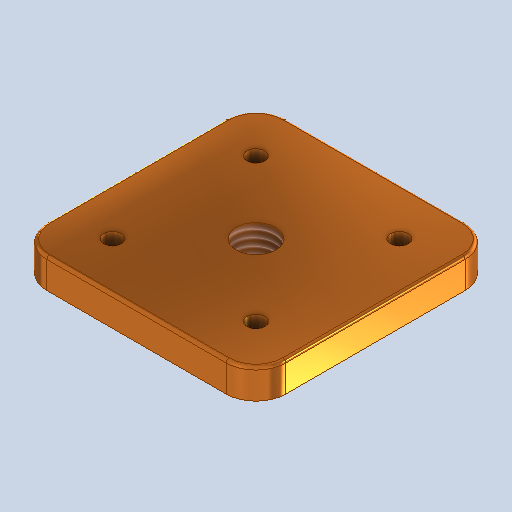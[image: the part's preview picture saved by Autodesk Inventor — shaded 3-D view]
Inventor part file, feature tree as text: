
AUTODESK INVENTOR PART (.ipt)
format: ipt  version: 2025.1 (Build 291241000, 241)  size: 265,728 bytes
history: native  units: mm
features: sketch x2, hole x2, fillet x2, extrude x1
ambient origin geometry x8: Origin, YZ Plane, XZ Plane, XY Plane, X Axis, Y Axis, Z Axis, Center Point
bodies: Solid1 (feature_tree)
feature tree (7):
  extrude  "Extrusion1"  Depth=40.0mm
  sketch  "Sketch2"  dims[d2=5.0mm d3=0.0mm d4=24.0mm d5=12.0mm d6=24.0mm d7=12.0mm d8=3.0mm d9=6.0mm d10=4.0mm d11=2.0mm d12=90.0deg d13=8.0mm d14=0.0mm d15=6.647mm d16=16.0mm d17=4.0mm d18=2.0mm d19=90.0deg d20=8.0mm d21=0.0mm d22=5.0mm d23=0.5mm]
  hole  "Hole1"  [1 undecoded]
  hole  "Hole2"  [1 undecoded]
  fillet  "Fillet1"  Radius=24.0mm
  fillet  "Fillet2"  Radius=12.0mm
  sketch  "Sketch1"  dims[d0=40.0mm d1=40.0mm]
note: 2 required parameter values undecoded (feature->parameter linkage not recoverable at this tier; creation-order binding heuristic only, values carry confidence <= 0.55)
